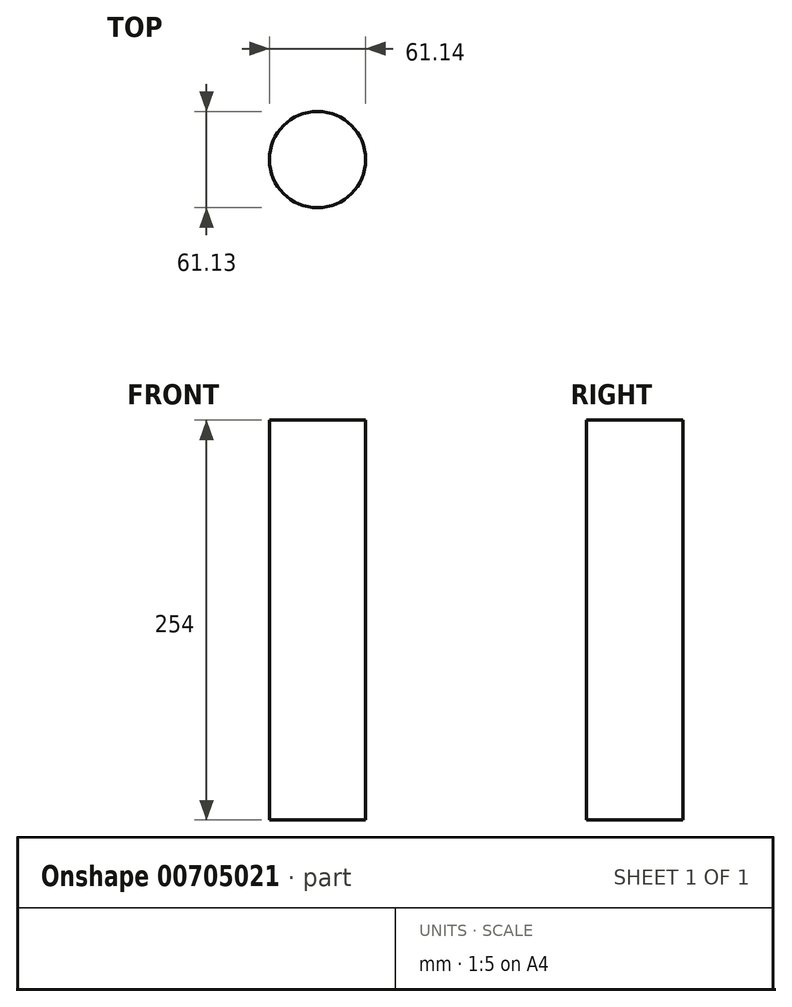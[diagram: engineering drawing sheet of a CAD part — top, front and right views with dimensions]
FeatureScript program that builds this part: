
annotation { "Feature Type Name" : "Feature", "Feature Type Description" : "" }
export const myFeature = defineFeature(function(context is Context, id is Id, definition is map)
    precondition{}
    {
        {
            var Q0;
            Q0=qCreatedBy(makeId("Top.planeOp"),FACE);
            var sketch = newSketch(context, id + "F0", { "sketchPlane" : qUnion([Q0])});
            skCircle(sketch, "E0", {"center": v(-39.6, 5.3) * mm, "radius": 30.57 * mm});
            skSolve(sketch);
        }
        {
            var Q0;
            Q0 = qSketchRegion(id + "F0", true);
            extrude(context, id + "F1", {"entities" : qUnion([Q0]), "endBound" : BoundingType.SYMMETRIC, "depth" : 254 * mm, "offsetDistance" : 25.4 * mm});
        }
    });
